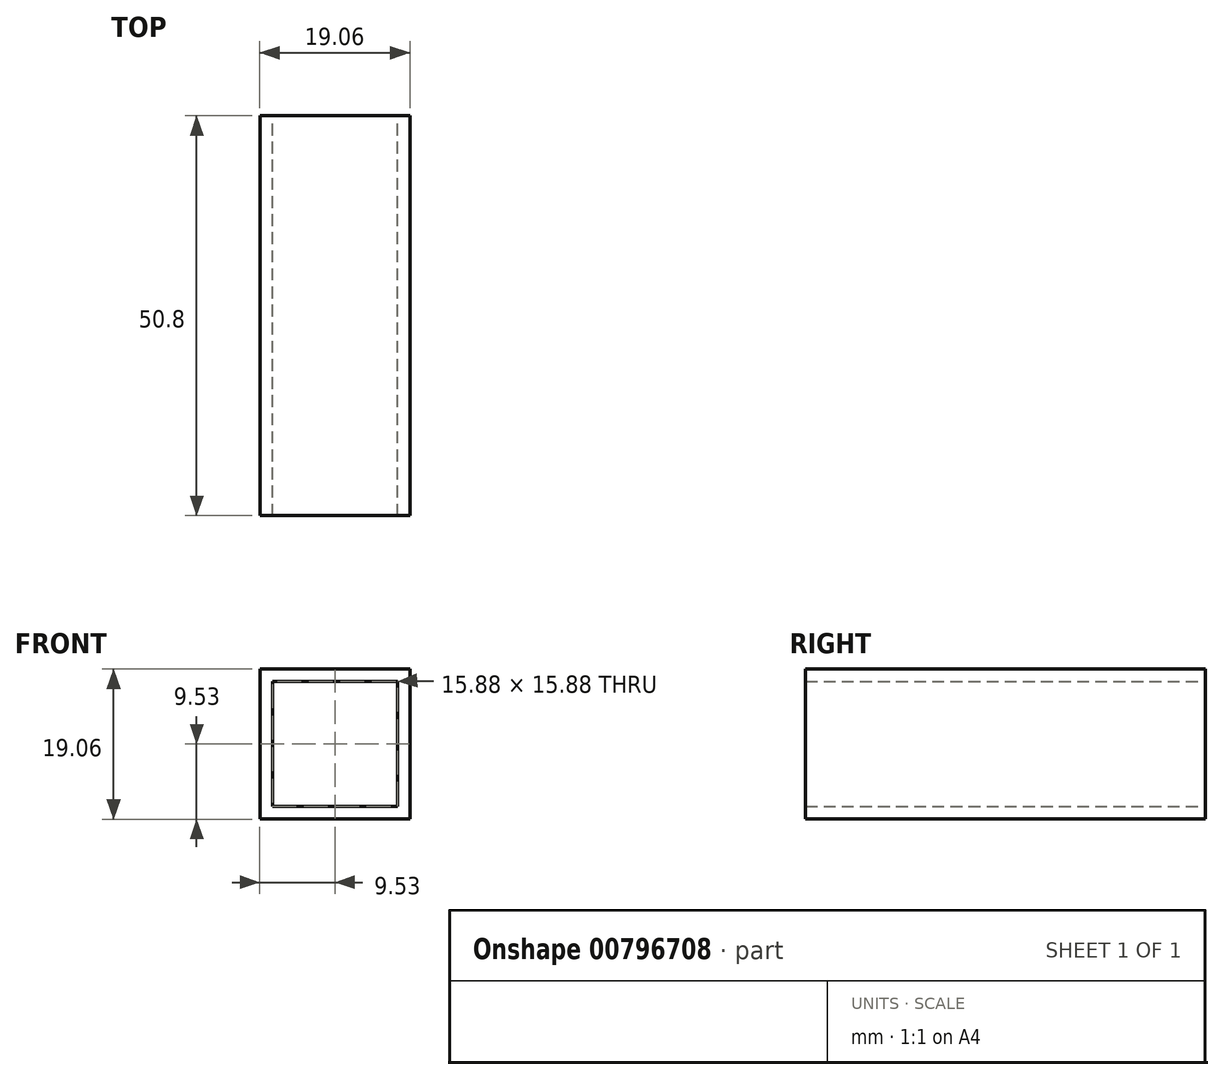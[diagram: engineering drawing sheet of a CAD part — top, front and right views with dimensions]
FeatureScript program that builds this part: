
annotation { "Feature Type Name" : "Feature", "Feature Type Description" : "" }
export const myFeature = defineFeature(function(context is Context, id is Id, definition is map)
    precondition{}
    {
        {
            var Q0;
            Q0=qCreatedBy(makeId("Front.planeOp"),FACE);
            var sketch = newSketch(context, id + "F0", { "sketchPlane" : qUnion([Q0])});
            skLineSegment(sketch, "E0.bottom", {"start": v(-9.52, 9.53) * mm, "end": v(9.53, 9.53) * mm});
            skLineSegment(sketch, "E0.top", {"start": v(-9.53, -9.53) * mm, "end": v(9.52, -9.53) * mm});
            skLineSegment(sketch, "E0.left", {"start": v(-9.52, 9.53) * mm, "end": v(-9.53, -9.52) * mm});
            skLineSegment(sketch, "E0.right", {"start": v(9.53, 9.53) * mm, "end": v(9.52, -9.52) * mm});
            skPoint(sketch, "E0.middle", {"position": v(0, 0) * mm});
            skLineSegment(sketch, "E1.bottom", {"start": v(-7.94, 7.94) * mm, "end": v(7.94, 7.94) * mm});
            skLineSegment(sketch, "E1.top", {"start": v(-7.94, -7.94) * mm, "end": v(7.94, -7.94) * mm});
            skLineSegment(sketch, "E1.left", {"start": v(-7.94, 7.94) * mm, "end": v(-7.94, -7.94) * mm});
            skLineSegment(sketch, "E1.right", {"start": v(7.94, 7.94) * mm, "end": v(7.94, -7.94) * mm});
            skSolve(sketch);
        }
        {
            var Q0;
            Q0=qSketchRegion(id+"F0",true);
            extrude(context, id + "F1", {"entities" : qUnion([Q0]), "depth" : 50.8 * mm, "offsetDistance" : 25.4 * mm});
        }
    });
